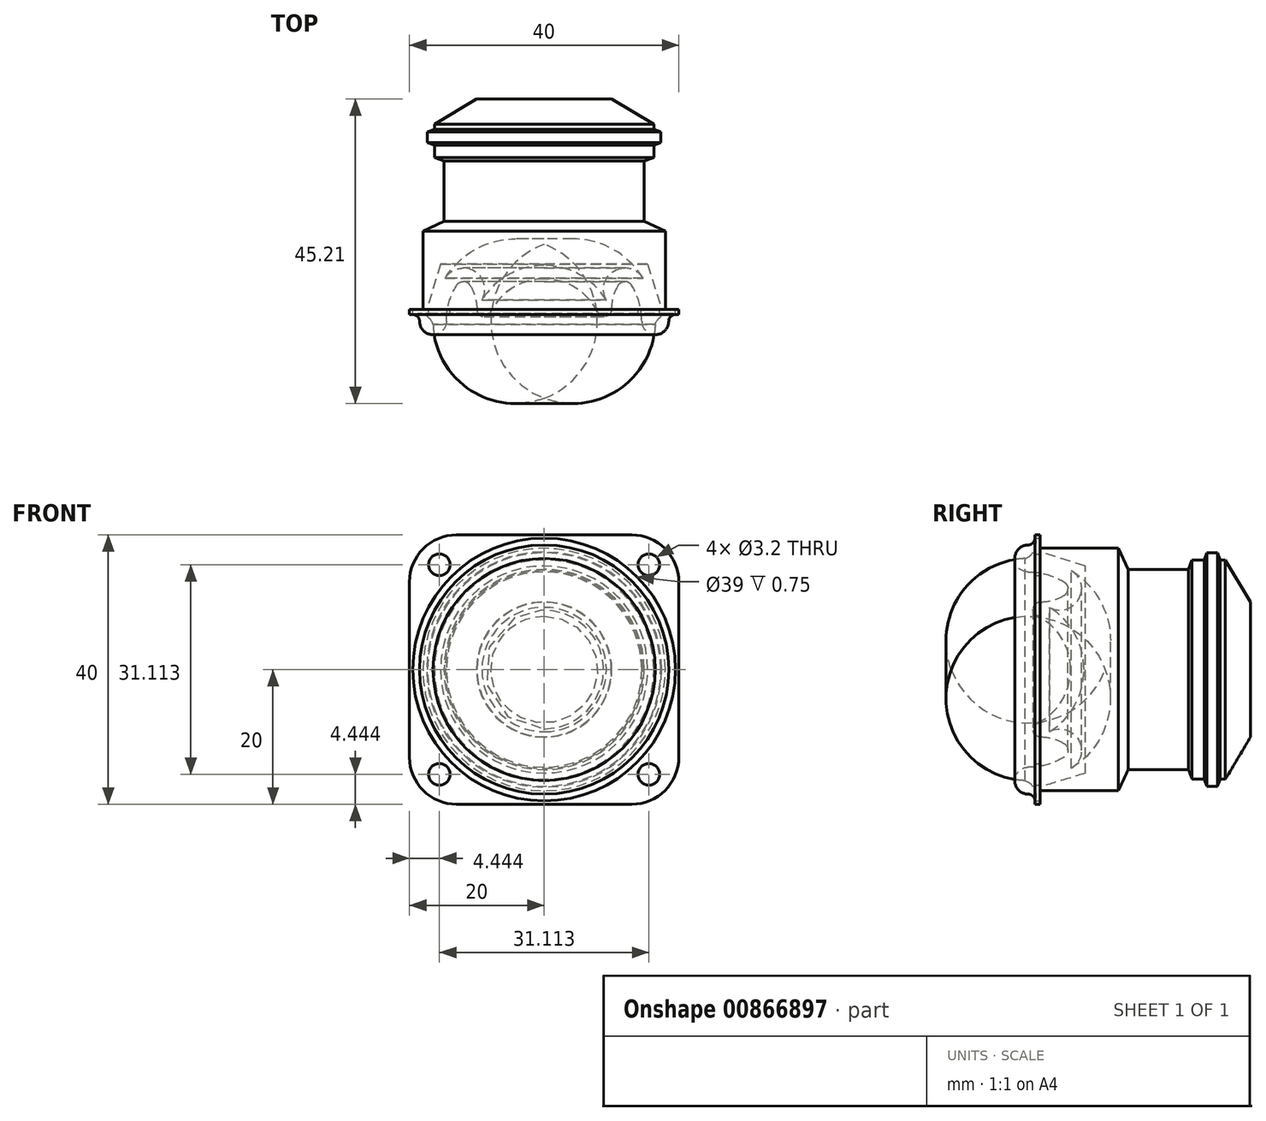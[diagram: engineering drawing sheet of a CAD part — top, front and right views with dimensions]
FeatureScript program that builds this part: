
annotation { "Feature Type Name" : "Feature", "Feature Type Description" : "" }
export const myFeature = defineFeature(function(context is Context, id is Id, definition is map)
    precondition{}
    {
        {
            var Q0;
            Q0=qCreatedBy(makeId("Front.planeOp"),FACE);
            var sketch = newSketch(context, id + "F0", { "sketchPlane" : qUnion([Q0])});
            skLineSegment(sketch, "E0.bottom", {"start": v(-13, -20) * mm, "end": v(13, -20) * mm});
            skLineSegment(sketch, "E0.top", {"start": v(-13, 20) * mm, "end": v(13, 20) * mm});
            skLineSegment(sketch, "E0.left", {"start": v(-20, -13) * mm, "end": v(-20, 13) * mm});
            skLineSegment(sketch, "E0.right", {"start": v(20, -13) * mm, "end": v(20, 13) * mm});
            skPoint(sketch, "E0.middle", {"position": v(0, 0) * mm});
            skPoint(sketch, "E1.visualSharp", {"position": v(-20, 20) * mm});
            skArc(sketch, "E1.filletArc", {"start": v(-13, 20) * mm, "mid": v(-17.95, 17.95) * mm, "end": v(-20, 13) * mm});
            skPoint(sketch, "E2.visualSharp", {"position": v(-20, -20) * mm});
            skArc(sketch, "E2.filletArc", {"start": v(-20, -13) * mm, "mid": v(-17.95, -17.95) * mm, "end": v(-13, -20) * mm});
            skPoint(sketch, "E3.visualSharp", {"position": v(20, -20) * mm});
            skArc(sketch, "E3.filletArc", {"start": v(13, -20) * mm, "mid": v(17.95, -17.95) * mm, "end": v(20, -13) * mm});
            skPoint(sketch, "E4.visualSharp", {"position": v(20, 20) * mm});
            skArc(sketch, "E4.filletArc", {"start": v(20, 13) * mm, "mid": v(17.95, 17.95) * mm, "end": v(13, 20) * mm});
            skCircle(sketch, "E5", {"center": v(15.56, 15.56) * mm, "radius": 1.6 * mm});
            skLineSegment(sketch, "E6", {"start": v(0, 0) * mm, "end": v(20, 20) * mm, "construction": true});
            skCircle(sketch, "E7.1.0", {"center": v(-15.56, 15.56) * mm, "radius": 1.6 * mm});
            skCircle(sketch, "E7.2.0", {"center": v(-15.56, -15.56) * mm, "radius": 1.6 * mm});
            skCircle(sketch, "E7.3.0", {"center": v(15.56, -15.56) * mm, "radius": 1.6 * mm});
            skCircle(sketch, "E8", {"center": v(0, 0) * mm, "radius": 19.5 * mm});
            skSolve(sketch);
        }
        {
            var Q0;
            Q0 = qSketchRegion(id + "F0", true);
            extrude(context, id + "F1", {"entities" : qUnion([Q0]), "depth" : .75 * mm, "offsetDistance" : 25 * mm});
        }
        {
            var Q0;
            Q0=qCreatedBy(makeId("Top.planeOp"),FACE);
            var sketch = newSketch(context, id + "F2", { "sketchPlane" : qUnion([Q0])});
            skLineSegment(sketch, "E9", {"start": v(0, 4.54) * mm, "end": v(1.75, 4.54) * mm, "construction": true});
            skArc(sketch, "E10", {"start": v(0, 4.54) * mm, "mid": v(-4.71, 3.18) * mm, "end": v(-7.99, -0.46) * mm});
            skArc(sketch, "E11", {"start": v(-7.99, -0.46) * mm, "mid": v(-9.17, -1.03) * mm, "end": v(-9.99, 0) * mm});
            skArc(sketch, "E12", {"start": v(-9.99, 0) * mm, "mid": v(-10.24, 1.86) * mm, "end": v(-11, 3.58) * mm});
            skArc(sketch, "E13", {"start": v(-11, 3.58) * mm, "mid": v(-12, 4.14) * mm, "end": v(-13, 3.58) * mm});
            skArc(sketch, "E14", {"start": v(-13, 3.58) * mm, "mid": v(-14.12, 1.02) * mm, "end": v(-14.5, -1.75) * mm});
            skArc(sketch, "E15", {"start": v(-14.5, -1.75) * mm, "mid": v(-16.5, -3.75) * mm, "end": v(-18.5, -1.75) * mm});
            skArc(sketch, "E16", {"start": v(-18.5, -1.75) * mm, "mid": v(-18.8, -1.04) * mm, "end": v(-19.5, -0.75) * mm});
            skLineSegment(sketch, "E17", {"start": v(-19.5, -0.75) * mm, "end": v(-20, -0.75) * mm, "construction": true});
            skArc(sketch, "E18.0", {"start": v(-16.5, -2.22) * mm, "mid": v(-17.7, -0.86) * mm, "end": v(-19.5, -0.75) * mm});
            skArc(sketch, "E18.1", {"start": v(-14.7, 4.63) * mm, "mid": v(-16.1, 1.34) * mm, "end": v(-16.5, -2.22) * mm});
            skArc(sketch, "E18.2", {"start": v(-9.24, 1.4) * mm, "mid": v(-10.39, 5.7) * mm, "end": v(-14.7, 4.63) * mm});
            skArc(sketch, "E18.3", {"start": v(0, 6.54) * mm, "mid": v(-5.28, 5.17) * mm, "end": v(-9.24, 1.4) * mm});
            skLineSegment(sketch, "E19", {"start": v(0, 4.54) * mm, "end": v(0, 6.54) * mm});
            skSolve(sketch);
        }
        {
            var Q0;
            Q0=makeQuery(id+"F2.imprint","IMPRINT",FACE,{"disambiguationData":[TD([[makeQuery(id+"F2.imprint","IMPRINT",EDGE,{"derivedFrom":sQuery(id+"F2.wireOp",EDGE,"E10")}),-1.0]])]});
            var Q1;
            Q1=sQuery(id+"F2.wireOp",EDGE,"E19");
            revolve(context, id + "F3", {"surfaceOperationType" : NewSurfaceOperationType.NEW, "entities" : qUnion([Q0]), "axis" : qUnion([Q1]), "revolveType" : RevolveType.FULL});
        }
        {
            var Q0;
            Q0=qCreatedBy(makeId("Top.planeOp"),FACE);
            var sketch = newSketch(context, id + "F4", { "sketchPlane" : qUnion([Q0])});
            skLineSegment(sketch, "E20", {"start": v(0, 6.71) * mm, "end": v(0, 31.25) * mm});
            skLineSegment(sketch, "E21", {"start": v(0, 31.25) * mm, "end": v(-10.04, 31.25) * mm});
            skLineSegment(sketch, "E22", {"start": v(-10.04, 31.25) * mm, "end": v(-16.28, 27.52) * mm});
            skLineSegment(sketch, "E23", {"start": v(-16.28, 27.52) * mm, "end": v(-16.28, 26.75) * mm});
            skLineSegment(sketch, "E24", {"start": v(-16.28, 26.75) * mm, "end": v(-17.32, 26.37) * mm});
            skLineSegment(sketch, "E25", {"start": v(-17.32, 26.37) * mm, "end": v(-17.32, 24.76) * mm});
            skLineSegment(sketch, "E26", {"start": v(-17.32, 24.76) * mm, "end": v(-16.28, 24.38) * mm});
            skLineSegment(sketch, "E27", {"start": v(-16.28, 24.38) * mm, "end": v(-16.28, 22.57) * mm});
            skLineSegment(sketch, "E28", {"start": v(-14.87, 22.06) * mm, "end": v(-16.28, 22.57) * mm});
            skLineSegment(sketch, "E29", {"start": v(-14.87, 22.06) * mm, "end": v(-14.87, 13.07) * mm});
            skLineSegment(sketch, "E30", {"start": v(-14.87, 13.07) * mm, "end": v(-18, 11.6) * mm});
            skLineSegment(sketch, "E31", {"start": v(-18, 11.6) * mm, "end": v(-18, 0) * mm});
            skLineSegment(sketch, "E32", {"start": v(-16.28, 25.57) * mm, "end": v(-17.32, 25.57) * mm, "construction": true});
            skLineSegment(sketch, "E33", {"start": v(-16.28, 26.75) * mm, "end": v(-16.28, 24.38) * mm, "construction": true});
            skPoint(sketch, "E34", {"position": v(-14.87, 22.06) * mm});
            skLineSegment(sketch, "E35", {"start": v(0, 6.71) * mm, "end": v(-15.38, 6.71) * mm});
            skLineSegment(sketch, "E36", {"start": v(-15.38, 6.71) * mm, "end": v(-17.45, 0) * mm});
            skLineSegment(sketch, "E37", {"start": v(-18, 0) * mm, "end": v(-17.45, 0) * mm});
            skSolve(sketch);
        }
        {
            var Q0;
            Q0 = qSketchRegion(id + "F4", true);
            var Q1;
            Q1=sQuery(id+"F4.wireOp",EDGE,"E20");
            revolve(context, id + "F5", {"operationType" : NewBodyOperationType.ADD, "surfaceOperationType" : NewSurfaceOperationType.NEW, "entities" : qUnion([Q0]), "axis" : qUnion([Q1]), "revolveType" : RevolveType.FULL});
        }
    });
